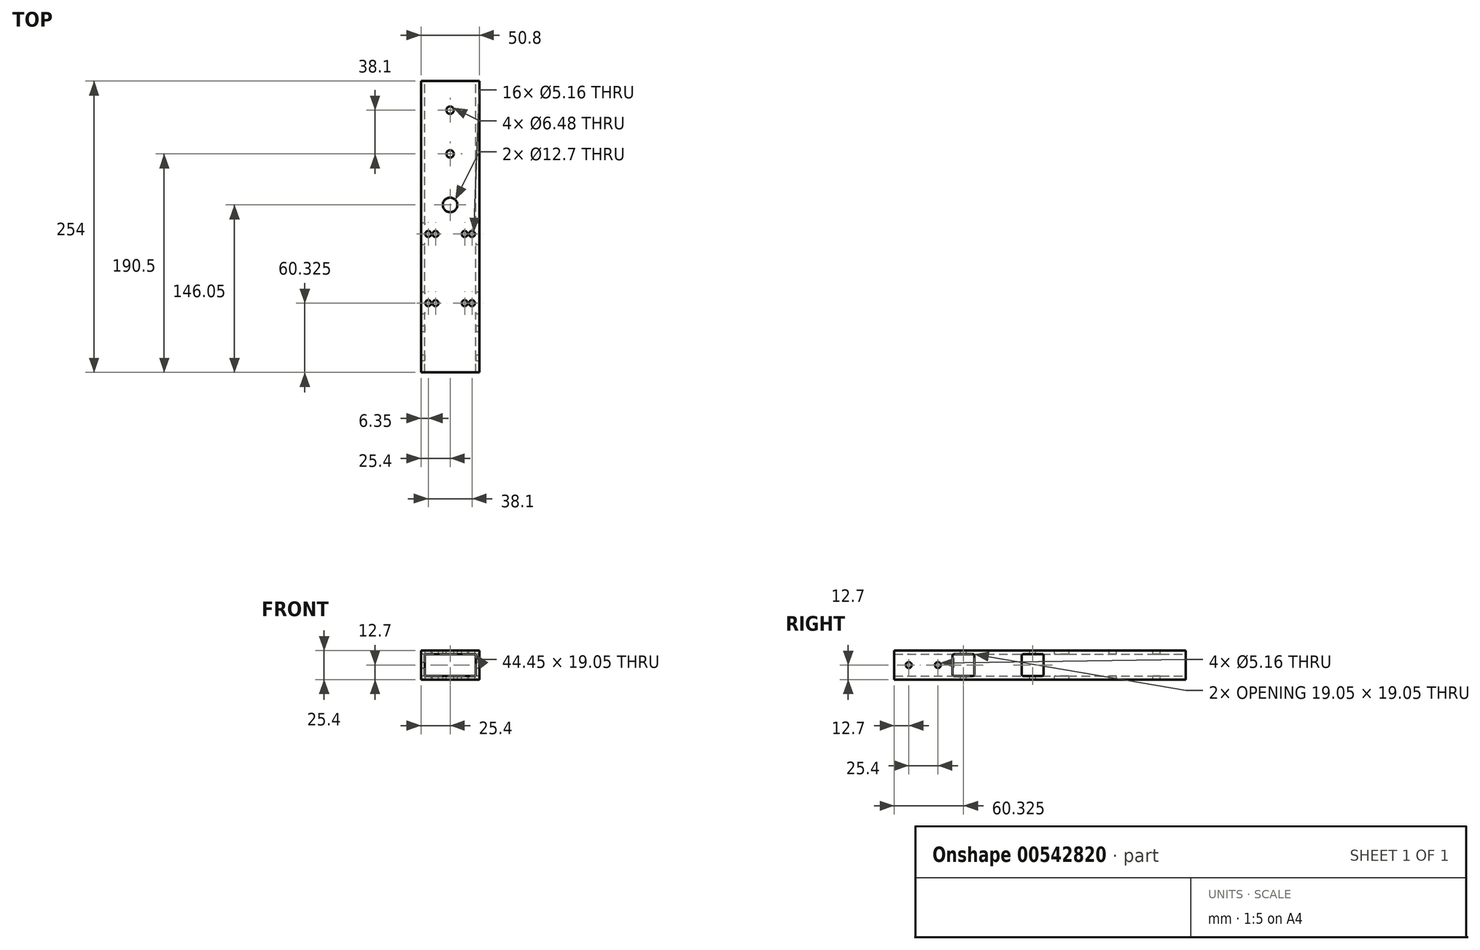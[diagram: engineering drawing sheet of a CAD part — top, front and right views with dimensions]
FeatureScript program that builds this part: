
annotation { "Feature Type Name" : "Feature", "Feature Type Description" : "" }
export const myFeature = defineFeature(function(context is Context, id is Id, definition is map)
    precondition{}
    {
        {
            var Q0;
            Q0=qCreatedBy(makeId("Front.planeOp"),FACE);
            var sketch = newSketch(context, id + "F0", { "sketchPlane" : qUnion([Q0])});
            skLineSegment(sketch, "E0.bottom", {"start": v(-50.8, 25.4) * mm, "end": v(0, 25.4) * mm});
            skLineSegment(sketch, "E0.top", {"start": v(-50.8, 0) * mm, "end": v(0, 0) * mm});
            skLineSegment(sketch, "E0.left", {"start": v(-50.8, 25.4) * mm, "end": v(-50.8, 0) * mm});
            skLineSegment(sketch, "E0.right", {"start": v(0, 25.4) * mm, "end": v(0, 0) * mm});
            skLineSegment(sketch, "E1.bottom", {"start": v(-47.63, 22.22) * mm, "end": v(-3.18, 22.22) * mm});
            skLineSegment(sketch, "E1.top", {"start": v(-47.63, 3.18) * mm, "end": v(-3.17, 3.18) * mm});
            skLineSegment(sketch, "E1.left", {"start": v(-47.63, 22.23) * mm, "end": v(-47.63, 3.18) * mm});
            skLineSegment(sketch, "E1.right", {"start": v(-3.18, 22.22) * mm, "end": v(-3.18, 3.18) * mm});
            skSolve(sketch);
        }
        {
            var Q0;
            Q0=makeQuery(id+"F0.imprint","IMPRINT",FACE,{"disambiguationData":[TD([[makeQuery(id+"F0.imprint","IMPRINT",EDGE,{"derivedFrom":sQuery(id+"F0.wireOp",EDGE,"E0.bottom")}),-1.0]])]});
            extrude(context, id + "F1", {"entities" : qUnion([Q0]), "depth" : 254 * mm});
        }
        {
            var Q0;
            Q0=makeQuery(id+"F1.opExtrude","SWEPT_FACE",FACE,{"disambiguationData":[OSD([sQuery(id+"F0.wireOp",EDGE,"E0.bottom")])]});
            var sketch = newSketch(context, id + "F2", { "sketchPlane" : qUnion([Q0])});
            skCircle(sketch, "E2", {"center": v(-25.4, -25.4) * mm, "radius": 3.24 * mm});
            skPoint(sketch, "E2.centerSnap0", {"position": v(-25.4, 0) * mm});
            skCircle(sketch, "E3", {"center": v(-25.4, -63.5) * mm, "radius": 3.24 * mm});
            skCircle(sketch, "E4", {"center": v(-25.4, -107.95) * mm, "radius": 6.35 * mm});
            skCircle(sketch, "E5", {"center": v(-44.45, -133.35) * mm, "radius": 2.58 * mm});
            skCircle(sketch, "E6", {"center": v(-38.1, -133.35) * mm, "radius": 2.58 * mm});
            skCircle(sketch, "E7", {"center": v(-12.7, -133.35) * mm, "radius": 2.58 * mm});
            skCircle(sketch, "E8", {"center": v(-6.35, -133.35) * mm, "radius": 2.58 * mm});
            skCircle(sketch, "E9", {"center": v(-44.45, -193.68) * mm, "radius": 2.58 * mm});
            skCircle(sketch, "E10", {"center": v(-38.1, -193.68) * mm, "radius": 2.58 * mm});
            skCircle(sketch, "E11", {"center": v(-12.7, -193.68) * mm, "radius": 2.58 * mm});
            skCircle(sketch, "E12", {"center": v(-6.35, -193.68) * mm, "radius": 2.58 * mm});
            skSolve(sketch);
        }
        {
            var Q0;
            Q0=makeQuery(id+"F2.imprint","IMPRINT",FACE,{"disambiguationData":[TD([[makeQuery(id+"F2.imprint","IMPRINT",EDGE,{"derivedFrom":sQuery(id+"F2.wireOp",EDGE,"E3")}),1.0]])]});
            var Q1;
            Q1=makeQuery(id+"F2.imprint","IMPRINT",FACE,{"disambiguationData":[TD([[makeQuery(id+"F2.imprint","IMPRINT",EDGE,{"derivedFrom":sQuery(id+"F2.wireOp",EDGE,"E2")}),1.0]])]});
            var Q2;
            Q2=makeQuery(id+"F2.imprint","IMPRINT",FACE,{"disambiguationData":[TD([[makeQuery(id+"F2.imprint","IMPRINT",EDGE,{"derivedFrom":sQuery(id+"F2.wireOp",EDGE,"E4")}),1.0]])]});
            var Q3;
            Q3=makeQuery(id+"F2.imprint","IMPRINT",FACE,{"disambiguationData":[TD([[makeQuery(id+"F2.imprint","IMPRINT",EDGE,{"derivedFrom":sQuery(id+"F2.wireOp",EDGE,"E5")}),1.0]])]});
            var Q4;
            Q4=makeQuery(id+"F2.imprint","IMPRINT",FACE,{"disambiguationData":[TD([[makeQuery(id+"F2.imprint","IMPRINT",EDGE,{"derivedFrom":sQuery(id+"F2.wireOp",EDGE,"E6")}),1.0]])]});
            var Q5;
            Q5=makeQuery(id+"F2.imprint","IMPRINT",FACE,{"disambiguationData":[TD([[makeQuery(id+"F2.imprint","IMPRINT",EDGE,{"derivedFrom":sQuery(id+"F2.wireOp",EDGE,"E7")}),1.0]])]});
            var Q6;
            Q6=makeQuery(id+"F2.imprint","IMPRINT",FACE,{"disambiguationData":[TD([[makeQuery(id+"F2.imprint","IMPRINT",EDGE,{"derivedFrom":sQuery(id+"F2.wireOp",EDGE,"E8")}),1.0]])]});
            var Q7;
            Q7=makeQuery(id+"F2.imprint","IMPRINT",FACE,{"disambiguationData":[TD([[makeQuery(id+"F2.imprint","IMPRINT",EDGE,{"derivedFrom":sQuery(id+"F2.wireOp",EDGE,"E9")}),1.0]])]});
            var Q8;
            Q8=makeQuery(id+"F2.imprint","IMPRINT",FACE,{"disambiguationData":[TD([[makeQuery(id+"F2.imprint","IMPRINT",EDGE,{"derivedFrom":sQuery(id+"F2.wireOp",EDGE,"E10")}),1.0]])]});
            var Q9;
            Q9=makeQuery(id+"F2.imprint","IMPRINT",FACE,{"disambiguationData":[TD([[makeQuery(id+"F2.imprint","IMPRINT",EDGE,{"derivedFrom":sQuery(id+"F2.wireOp",EDGE,"E11")}),1.0]])]});
            var Q10;
            Q10=makeQuery(id+"F2.imprint","IMPRINT",FACE,{"disambiguationData":[TD([[makeQuery(id+"F2.imprint","IMPRINT",EDGE,{"derivedFrom":sQuery(id+"F2.wireOp",EDGE,"E12")}),1.0]])]});
            extrude(context, id + "F3", {"entities" : qUnion([Q0, Q1, Q2, Q3, Q4, Q5, Q6, Q7, Q8, Q9, Q10]), "operationType" : NewBodyOperationType.REMOVE, "oppositeDirection" : true, "depth" : 25.4 * mm, "offsetDistance" : 25.4 * mm});
        }
        {
            var Q0;
            Q0=makeQuery(id+"F1.opExtrude","SWEPT_FACE",FACE,{"disambiguationData":[OSD([sQuery(id+"F0.wireOp",EDGE,"E0.right")])]});
            var sketch = newSketch(context, id + "F4", { "sketchPlane" : qUnion([Q0])});
            skCircle(sketch, "E13", {"center": v(-241.3, 12.7) * mm, "radius": 2.58 * mm});
            skPoint(sketch, "E13.centerSnap0", {"position": v(-254, 12.7) * mm});
            skCircle(sketch, "E14", {"center": v(-215.9, 12.7) * mm, "radius": 2.58 * mm});
            skSolve(sketch);
        }
        {
            var Q0;
            Q0=makeQuery(id+"F4.imprint","IMPRINT",FACE,{"disambiguationData":[TD([[makeQuery(id+"F4.imprint","IMPRINT",EDGE,{"derivedFrom":sQuery(id+"F4.wireOp",EDGE,"E13")}),1.0]])]});
            var Q1;
            Q1=makeQuery(id+"F4.imprint","IMPRINT",FACE,{"disambiguationData":[TD([[makeQuery(id+"F4.imprint","IMPRINT",EDGE,{"derivedFrom":sQuery(id+"F4.wireOp",EDGE,"E14")}),1.0]])]});
            extrude(context, id + "F5", {"entities" : qUnion([Q0, Q1]), "operationType" : NewBodyOperationType.REMOVE, "endBound" : BoundingType.THROUGH_ALL, "oppositeDirection" : true, "depth" : 25.4 * mm, "offsetDistance" : 25.4 * mm});
        }
        {
            var Q0;
            Q0=makeQuery(id+"F1.opExtrude","SWEPT_FACE",FACE,{"disambiguationData":[OSD([sQuery(id+"F0.wireOp",EDGE,"E0.left")])]});
            var sketch = newSketch(context, id + "F6", { "sketchPlane" : qUnion([Q0])});
            skLineSegment(sketch, "E15.bottom", {"start": v(125.36, 22.23) * mm, "end": v(141.34, 22.23) * mm});
            skLineSegment(sketch, "E15.top", {"start": v(125.36, 3.18) * mm, "end": v(141.34, 3.18) * mm});
            skLineSegment(sketch, "E15.left", {"start": v(123.83, 20.7) * mm, "end": v(123.83, 4.7) * mm});
            skLineSegment(sketch, "E15.right", {"start": v(142.88, 20.7) * mm, "end": v(142.88, 4.7) * mm});
            skArc(sketch, "E16", {"start": v(123.83, 20.7) * mm, "mid": v(124.27, 21.78) * mm, "end": v(125.36, 22.23) * mm});
            skArc(sketch, "E17", {"start": v(142.88, 20.7) * mm, "mid": v(142.43, 21.78) * mm, "end": v(141.34, 22.23) * mm});
            skArc(sketch, "E18", {"start": v(142.88, 4.7) * mm, "mid": v(142.43, 3.62) * mm, "end": v(141.34, 3.18) * mm});
            skArc(sketch, "E19", {"start": v(125.36, 3.18) * mm, "mid": v(124.27, 3.62) * mm, "end": v(123.83, 4.7) * mm});
            skLineSegment(sketch, "E20.bottom", {"start": v(185.68, 22.22) * mm, "end": v(201.67, 22.22) * mm});
            skLineSegment(sketch, "E20.top", {"start": v(185.68, 3.18) * mm, "end": v(201.67, 3.18) * mm});
            skLineSegment(sketch, "E20.left", {"start": v(184.15, 20.7) * mm, "end": v(184.15, 4.7) * mm});
            skLineSegment(sketch, "E20.right", {"start": v(203.2, 20.7) * mm, "end": v(203.2, 4.7) * mm});
            skArc(sketch, "E21", {"start": v(184.15, 20.7) * mm, "mid": v(184.6, 21.78) * mm, "end": v(185.68, 22.22) * mm});
            skArc(sketch, "E22", {"start": v(203.2, 20.7) * mm, "mid": v(202.75, 21.78) * mm, "end": v(201.67, 22.22) * mm});
            skArc(sketch, "E23", {"start": v(203.2, 4.7) * mm, "mid": v(202.75, 3.62) * mm, "end": v(201.67, 3.17) * mm});
            skArc(sketch, "E24", {"start": v(185.68, 3.17) * mm, "mid": v(184.6, 3.62) * mm, "end": v(184.15, 4.7) * mm});
            skSolve(sketch);
        }
        {
            var Q0;
            Q0=makeQuery(id+"F6.imprint","IMPRINT",FACE,{"disambiguationData":[TD([[makeQuery(id+"F6.imprint","IMPRINT",EDGE,{"derivedFrom":sQuery(id+"F6.wireOp",EDGE,"E20.bottom")}),-1.0]])]});
            var Q1;
            Q1=makeQuery(id+"F6.imprint","IMPRINT",FACE,{"disambiguationData":[TD([[makeQuery(id+"F6.imprint","IMPRINT",EDGE,{"derivedFrom":sQuery(id+"F6.wireOp",EDGE,"E15.bottom")}),-1.0]])]});
            extrude(context, id + "F7", {"entities" : qUnion([Q0, Q1]), "operationType" : NewBodyOperationType.REMOVE, "endBound" : BoundingType.THROUGH_ALL, "oppositeDirection" : true, "depth" : 25.4 * mm, "offsetDistance" : 25.4 * mm});
        }
    });
